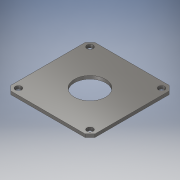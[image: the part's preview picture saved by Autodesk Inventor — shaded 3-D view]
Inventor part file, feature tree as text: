
AUTODESK INVENTOR PART (.ipt)
format: ipt  version: 2018 (Build 220112000, 112)  size: 134,656 bytes
history: native  units: in
note: dims shown in document units (in); Inventor stores cm internally (conversion verified against a paired STEP export)
features: sketch x4, extrude x2, hole x1
ambient origin geometry x8: Origin, YZ Plane, XZ Plane, XY Plane, X Axis, Y Axis, Z Axis, Center Point
bodies: Solid1 (feature_tree)
feature tree (7):
  extrude  "Extrusion1"  Depth=0.1in TaperAngle=0.0deg
  hole  "Hole1"  [1 undecoded]
  sketch  "Sketch3"  dims[d8=0.201in d9=0.5in d10=0.375in d11=0.25in d12=0.5635in d13=1.0in d14=0.8108in d15=0.2in]
  extrude  "Extrusion2"  Depth=0.5in
  sketch  "Sketch1"  dims[d0=1.0in d2=0.1in d3=0.0in]
  sketch  "Sketch2"  dims[d4=2.7in d5=2.7in]
  sketch  "Sketch4"  dims[d16=0.2in d17=3.0in d18=2.0in d19=3.756in d20=3.6in d21=1.0in d22=0.0in]
note: 1 required parameter value undecoded (feature->parameter linkage not recoverable at this tier; creation-order binding heuristic only, values carry confidence <= 0.55)
